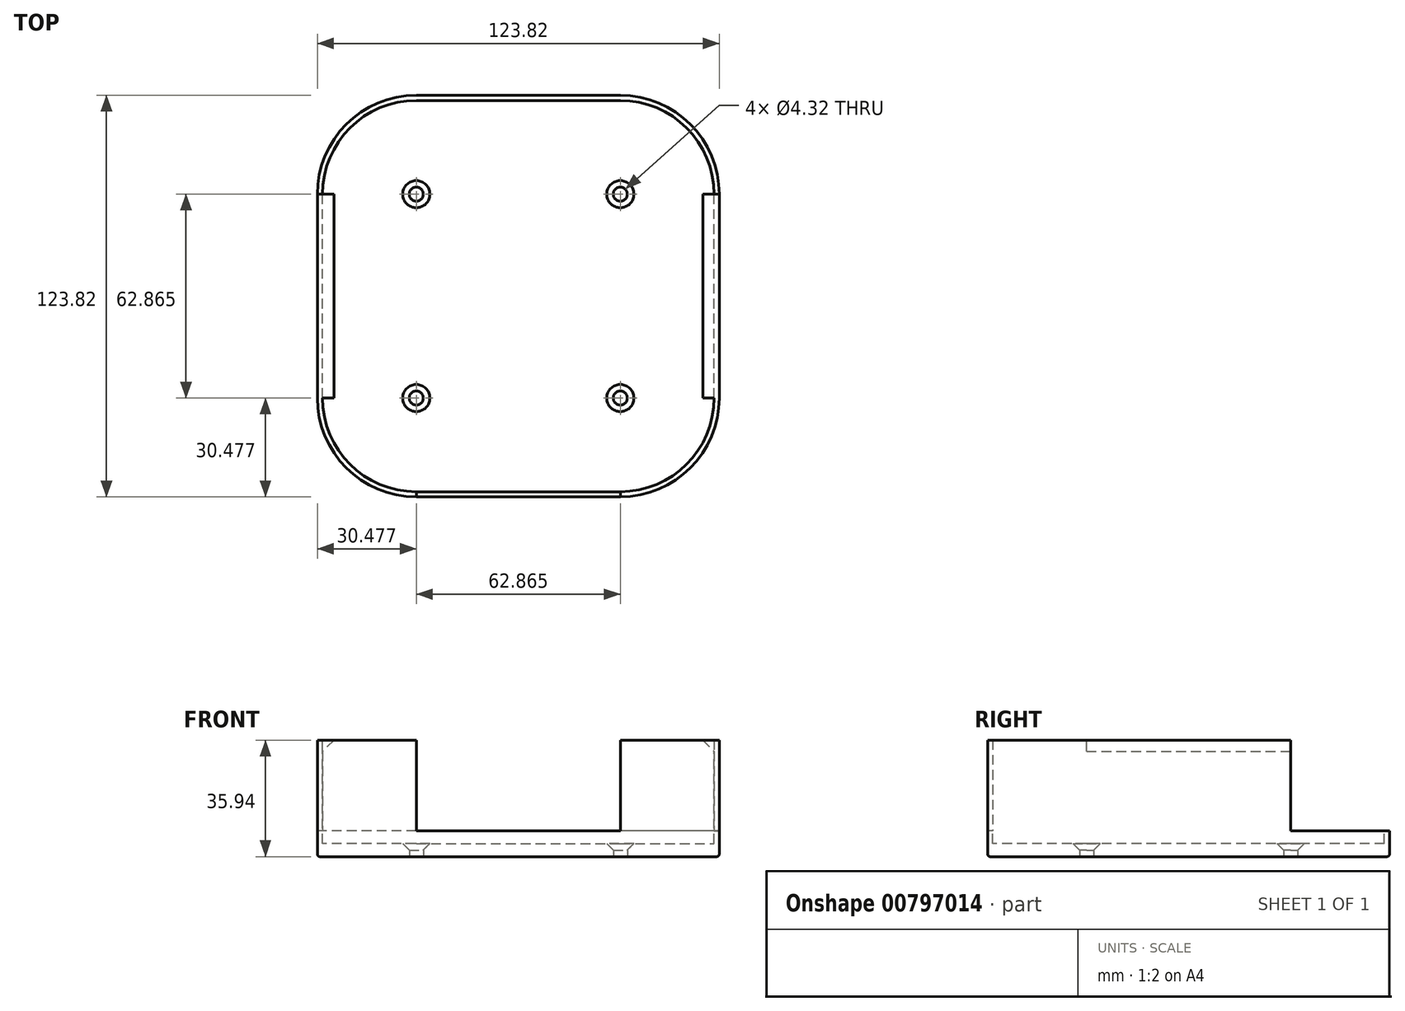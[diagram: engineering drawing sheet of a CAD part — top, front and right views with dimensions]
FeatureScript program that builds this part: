
annotation { "Feature Type Name" : "Feature", "Feature Type Description" : "" }
export const myFeature = defineFeature(function(context is Context, id is Id, definition is map)
    precondition{}
    {
        {
            var Q0;
            Q0=qCreatedBy(makeId("Top.planeOp"),FACE);
            var sketch = newSketch(context, id + "F0", { "sketchPlane" : qUnion([Q0])});
            skLineSegment(sketch, "E0.bottom", {"start": v(-31.43, 61.91) * mm, "end": v(31.43, 61.91) * mm});
            skLineSegment(sketch, "E0.top", {"start": v(-31.43, -61.91) * mm, "end": v(31.43, -61.91) * mm});
            skLineSegment(sketch, "E0.left", {"start": v(-61.91, 31.43) * mm, "end": v(-61.91, -31.43) * mm});
            skLineSegment(sketch, "E0.right", {"start": v(61.91, 31.43) * mm, "end": v(61.91, -31.43) * mm});
            skPoint(sketch, "E1.visualSharp", {"position": v(-61.91, 61.91) * mm});
            skArc(sketch, "E1.filletArc", {"start": v(-31.43, 61.91) * mm, "mid": v(-52.99, 52.99) * mm, "end": v(-61.91, 31.43) * mm});
            skPoint(sketch, "E2.visualSharp", {"position": v(61.91, 61.91) * mm});
            skArc(sketch, "E2.filletArc", {"start": v(61.91, 31.43) * mm, "mid": v(52.99, 52.99) * mm, "end": v(31.43, 61.91) * mm});
            skPoint(sketch, "E3.visualSharp", {"position": v(61.91, -61.91) * mm});
            skArc(sketch, "E3.filletArc", {"start": v(31.43, -61.91) * mm, "mid": v(52.99, -52.99) * mm, "end": v(61.91, -31.43) * mm});
            skPoint(sketch, "E4.visualSharp", {"position": v(-61.91, -61.91) * mm});
            skArc(sketch, "E4.filletArc", {"start": v(-61.91, -31.43) * mm, "mid": v(-52.99, -52.99) * mm, "end": v(-31.43, -61.91) * mm});
            skSolve(sketch);
        }
        {
            var Q0;
            Q0 = qSketchRegion(id + "F0", true);
            extrude(context, id + "F1", {"entities" : qUnion([Q0]), "depth" : 8 * mm, "offsetDistance" : 25.4 * mm});
        }
        {
            var Q0;
            Q0=makeQuery(id+"F1.opExtrude","CAP_FACE",FACE,{"disambiguationData":[OSD([sQuery(id+"F0.wireOp",EDGE,"E0.bottom"),sQuery(id+"F0.wireOp",EDGE,"E0.top"),sQuery(id+"F0.wireOp",EDGE,"E0.left"),sQuery(id+"F0.wireOp",EDGE,"E0.right"),sQuery(id+"F0.wireOp",EDGE,"E1.filletArc"),sQuery(id+"F0.wireOp",EDGE,"E2.filletArc"),sQuery(id+"F0.wireOp",EDGE,"E3.filletArc"),sQuery(id+"F0.wireOp",EDGE,"E4.filletArc")])],"isStart":false});
            var sketch = newSketch(context, id + "F2", { "sketchPlane" : qUnion([Q0])});
            skArc(sketch, "E5.0", {"start": v(-31.43, 60.33) * mm, "mid": v(-51.86, 51.86) * mm, "end": v(-60.33, 31.43) * mm});
            skLineSegment(sketch, "E5.1", {"start": v(-60.33, 31.43) * mm, "end": v(-60.33, -31.43) * mm});
            skLineSegment(sketch, "E5.2", {"start": v(-31.43, 60.33) * mm, "end": v(31.43, 60.33) * mm});
            skArc(sketch, "E5.3", {"start": v(-60.33, -31.43) * mm, "mid": v(-51.86, -51.86) * mm, "end": v(-31.43, -60.33) * mm});
            skArc(sketch, "E5.4", {"start": v(60.33, 31.43) * mm, "mid": v(51.86, 51.86) * mm, "end": v(31.43, 60.33) * mm});
            skLineSegment(sketch, "E5.5", {"start": v(60.33, 31.43) * mm, "end": v(60.33, -31.43) * mm});
            skArc(sketch, "E5.6", {"start": v(31.43, -60.32) * mm, "mid": v(51.86, -51.86) * mm, "end": v(60.33, -31.43) * mm});
            skLineSegment(sketch, "E5.7", {"start": v(-31.43, -60.33) * mm, "end": v(31.43, -60.33) * mm});
            skSolve(sketch);
        }
        {
            var Q0;
            Q0 = qSketchRegion(id + "F2", true);
            extrude(context, id + "F3", {"entities" : qUnion([Q0]), "operationType" : NewBodyOperationType.REMOVE, "oppositeDirection" : true, "depth" : 3.94 * mm, "offsetDistance" : 25.4 * mm});
        }
        {
            var Q0;
            Q0=makeQuery(id+"F1.opExtrude","CAP_FACE",FACE,{"disambiguationData":[OSD([sQuery(id+"F0.wireOp",EDGE,"E0.bottom"),sQuery(id+"F0.wireOp",EDGE,"E0.top"),sQuery(id+"F0.wireOp",EDGE,"E0.left"),sQuery(id+"F0.wireOp",EDGE,"E0.right"),sQuery(id+"F0.wireOp",EDGE,"E1.filletArc"),sQuery(id+"F0.wireOp",EDGE,"E2.filletArc"),sQuery(id+"F0.wireOp",EDGE,"E3.filletArc"),sQuery(id+"F0.wireOp",EDGE,"E4.filletArc")])],"isStart":false});
            var sketch = newSketch(context, id + "F4", { "sketchPlane" : qUnion([Q0])});
            skLineSegment(sketch, "E6", {"start": v(60.33, 31.43) * mm, "end": v(61.91, 31.43) * mm});
            skLineSegment(sketch, "E7", {"start": v(-60.33, 31.43) * mm, "end": v(-61.91, 31.43) * mm});
            skLineSegment(sketch, "E8", {"start": v(-31.43, -60.33) * mm, "end": v(-31.43, -61.91) * mm});
            skLineSegment(sketch, "E9", {"start": v(31.43, -60.32) * mm, "end": v(31.43, -61.91) * mm});
            skLineSegment(sketch, "E10.0", {"start": v(60.33, 31.43) * mm, "end": v(60.33, -31.43) * mm});
            skArc(sketch, "E11.0", {"start": v(31.43, -60.32) * mm, "mid": v(51.86, -51.86) * mm, "end": v(60.33, -31.43) * mm});
            skArc(sketch, "E12.0", {"start": v(31.43, -61.91) * mm, "mid": v(52.99, -52.99) * mm, "end": v(61.91, -31.43) * mm});
            skLineSegment(sketch, "E13.0", {"start": v(61.91, 31.43) * mm, "end": v(61.91, -31.43) * mm});
            skLineSegment(sketch, "E14.0", {"start": v(-60.33, 31.43) * mm, "end": v(-60.33, -31.43) * mm});
            skLineSegment(sketch, "E15.0", {"start": v(-61.91, 31.43) * mm, "end": v(-61.91, -31.43) * mm});
            skArc(sketch, "E16.0", {"start": v(-61.91, -31.43) * mm, "mid": v(-52.99, -52.99) * mm, "end": v(-31.43, -61.91) * mm});
            skArc(sketch, "E17.0", {"start": v(-60.33, -31.43) * mm, "mid": v(-51.86, -51.86) * mm, "end": v(-31.43, -60.33) * mm});
            skSolve(sketch);
        }
        {
            var Q0;
            Q0 = qSketchRegion(id + "F4", true);
            extrude(context, id + "F5", {"entities" : qUnion([Q0]), "operationType" : NewBodyOperationType.ADD, "depth" : 27.94 * mm, "offsetDistance" : 25.4 * mm});
        }
        {
            var Q0;
            Q0=makeQuery(id+"F5.opExtrude","SWEPT_FACE",FACE,{"disambiguationData":[OSD([sQuery(id+"F4.wireOp",EDGE,"E6")])]});
            var sketch = newSketch(context, id + "F6", { "sketchPlane" : qUnion([Q0])});
            skLineSegment(sketch, "E18", {"start": v(-60.33, 35.94) * mm, "end": v(-56.83, 35.94) * mm});
            skLineSegment(sketch, "E19", {"start": v(-56.83, 35.94) * mm, "end": v(-60.33, 32.45) * mm});
            skLineSegment(sketch, "E20", {"start": v(-60.33, 32.45) * mm, "end": v(-60.33, 35.94) * mm});
            skLineSegment(sketch, "E21.MirrorCS", {"start": v(60.32, 35.94) * mm, "end": v(56.83, 35.94) * mm});
            skLineSegment(sketch, "E22.MirrorCS", {"start": v(56.83, 35.94) * mm, "end": v(60.32, 32.45) * mm});
            skLineSegment(sketch, "E23.MirrorCS", {"start": v(60.32, 32.45) * mm, "end": v(60.32, 35.94) * mm});
            skSolve(sketch);
        }
        {
            var Q0;
            Q0 = qSketchRegion(id + "F6", true);
            var Q1;
            Q1=makeQuery(id+"F5.opExtrude","CAP_VERTEX",VERTEX,{"disambiguationData":[OSD([sQuery(id+"F4.wireOp",EDGE,"E10.0"),sQuery(id+"F4.wireOp",EDGE,"E11.0")])],"isStart":false});
            extrude(context, id + "F7", {"entities" : qUnion([Q0]), "operationType" : NewBodyOperationType.ADD, "endBound" : BoundingType.UP_TO_VERTEX, "oppositeDirection" : true, "depth" : 25.4 * mm, "endBoundEntityVertex" : qUnion([Q1]), "offsetDistance" : 25.4 * mm});
        }
        {
            var Q0;
            Q0=makeQuery(id+"F1.opExtrude","CAP_FACE",FACE,{"disambiguationData":[OSD([sQuery(id+"F0.wireOp",EDGE,"E0.bottom"),sQuery(id+"F0.wireOp",EDGE,"E0.top"),sQuery(id+"F0.wireOp",EDGE,"E0.left"),sQuery(id+"F0.wireOp",EDGE,"E0.right"),sQuery(id+"F0.wireOp",EDGE,"E1.filletArc"),sQuery(id+"F0.wireOp",EDGE,"E2.filletArc"),sQuery(id+"F0.wireOp",EDGE,"E3.filletArc"),sQuery(id+"F0.wireOp",EDGE,"E4.filletArc")])],"isStart":true});
            var sketch = newSketch(context, id + "F8", { "sketchPlane" : qUnion([Q0])});
            skCircle(sketch, "E24", {"center": v(-31.43, 31.43) * mm, "radius": 2.16 * mm});
            skCircle(sketch, "E25", {"center": v(31.43, 31.43) * mm, "radius": 2.16 * mm});
            skCircle(sketch, "E26", {"center": v(31.43, -31.43) * mm, "radius": 2.16 * mm});
            skCircle(sketch, "E27", {"center": v(-31.43, -31.43) * mm, "radius": 2.16 * mm});
            skSolve(sketch);
        }
        {
            var Q0;
            Q0 = qSketchRegion(id + "F8", true);
            extrude(context, id + "F9", {"entities" : qUnion([Q0]), "operationType" : NewBodyOperationType.REMOVE, "oppositeDirection" : true, "depth" : 25.4 * mm, "offsetDistance" : 25.4 * mm});
        }
        {
            var Q0;
            Q0=makeQuery(id+"F9.boolean.opBoolean","INTERSECT",EDGE,{"derivedFrom":[makeQuery(id+"F3.boolean.opBoolean","COPY",FACE,{"derivedFrom":makeQuery(id+"F3.opExtrude","CAP_FACE",FACE,{"disambiguationData":[OSD([sQuery(id+"F2.wireOp",EDGE,"E5.0"),sQuery(id+"F2.wireOp",EDGE,"E5.1"),sQuery(id+"F2.wireOp",EDGE,"E5.2"),sQuery(id+"F2.wireOp",EDGE,"E5.3"),sQuery(id+"F2.wireOp",EDGE,"E5.4"),sQuery(id+"F2.wireOp",EDGE,"E5.5"),sQuery(id+"F2.wireOp",EDGE,"E5.6"),sQuery(id+"F2.wireOp",EDGE,"E5.7")])],"isStart":false})}),makeQuery(id+"F9.opExtrude","SWEPT_FACE",FACE,{"disambiguationData":[OSD([sQuery(id+"F8.wireOp",EDGE,"E25")])]})]});
            var Q1;
            Q1=makeQuery(id+"F9.boolean.opBoolean","INTERSECT",EDGE,{"derivedFrom":[makeQuery(id+"F3.boolean.opBoolean","COPY",FACE,{"derivedFrom":makeQuery(id+"F3.opExtrude","CAP_FACE",FACE,{"disambiguationData":[OSD([sQuery(id+"F2.wireOp",EDGE,"E5.0"),sQuery(id+"F2.wireOp",EDGE,"E5.1"),sQuery(id+"F2.wireOp",EDGE,"E5.2"),sQuery(id+"F2.wireOp",EDGE,"E5.3"),sQuery(id+"F2.wireOp",EDGE,"E5.4"),sQuery(id+"F2.wireOp",EDGE,"E5.5"),sQuery(id+"F2.wireOp",EDGE,"E5.6"),sQuery(id+"F2.wireOp",EDGE,"E5.7")])],"isStart":false})}),makeQuery(id+"F9.opExtrude","SWEPT_FACE",FACE,{"disambiguationData":[OSD([sQuery(id+"F8.wireOp",EDGE,"E24")])]})]});
            var Q2;
            Q2=makeQuery(id+"F9.boolean.opBoolean","INTERSECT",EDGE,{"derivedFrom":[makeQuery(id+"F3.boolean.opBoolean","COPY",FACE,{"derivedFrom":makeQuery(id+"F3.opExtrude","CAP_FACE",FACE,{"disambiguationData":[OSD([sQuery(id+"F2.wireOp",EDGE,"E5.0"),sQuery(id+"F2.wireOp",EDGE,"E5.1"),sQuery(id+"F2.wireOp",EDGE,"E5.2"),sQuery(id+"F2.wireOp",EDGE,"E5.3"),sQuery(id+"F2.wireOp",EDGE,"E5.4"),sQuery(id+"F2.wireOp",EDGE,"E5.5"),sQuery(id+"F2.wireOp",EDGE,"E5.6"),sQuery(id+"F2.wireOp",EDGE,"E5.7")])],"isStart":false})}),makeQuery(id+"F9.opExtrude","SWEPT_FACE",FACE,{"disambiguationData":[OSD([sQuery(id+"F8.wireOp",EDGE,"E27")])]})]});
            var Q3;
            Q3=makeQuery(id+"F9.boolean.opBoolean","INTERSECT",EDGE,{"derivedFrom":[makeQuery(id+"F3.boolean.opBoolean","COPY",FACE,{"derivedFrom":makeQuery(id+"F3.opExtrude","CAP_FACE",FACE,{"disambiguationData":[OSD([sQuery(id+"F2.wireOp",EDGE,"E5.0"),sQuery(id+"F2.wireOp",EDGE,"E5.1"),sQuery(id+"F2.wireOp",EDGE,"E5.2"),sQuery(id+"F2.wireOp",EDGE,"E5.3"),sQuery(id+"F2.wireOp",EDGE,"E5.4"),sQuery(id+"F2.wireOp",EDGE,"E5.5"),sQuery(id+"F2.wireOp",EDGE,"E5.6"),sQuery(id+"F2.wireOp",EDGE,"E5.7")])],"isStart":false})}),makeQuery(id+"F9.opExtrude","SWEPT_FACE",FACE,{"disambiguationData":[OSD([sQuery(id+"F8.wireOp",EDGE,"E26")])]})]});
            chamfer(context, id + "F10", {"entities" : qUnion([Q0, Q1, Q2, Q3]), "width" : 2.03 * mm, "tangentPropagation" : true});
        }
        {
            var Q0;
            Q0=makeQuery(id+"F1.opExtrude","CAP_EDGE",EDGE,{"disambiguationData":[OSD([sQuery(id+"F0.wireOp",EDGE,"E1.filletArc")])],"isStart":true});
            fillet(context, id + "F11", {"entities" : qUnion([Q0]), "radius" : 0.76 * mm, "tangentPropagation" : true, "allowEdgeOverflow" : false});
        }
    });
